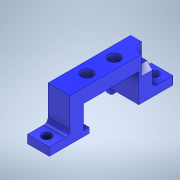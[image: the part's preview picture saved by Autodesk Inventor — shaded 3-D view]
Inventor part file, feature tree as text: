
AUTODESK INVENTOR PART (.ipt)
format: ipt  version: 2022.6 (Build 266554000, 554)  size: 222,208 bytes
history: native  units: mm
features: projected_geometry x6, sketch x5, extrude x4, hole x2, chamfer x2, fillet x1
ambient origin geometry x8: Origin, YZ Plane, XZ Plane, XY Plane, X Axis, Y Axis, Z Axis, Center Point
bodies: Solid1 (feature_tree)
feature tree (20):
  extrude  "Extrusion1"  Depth=5.0mm
  hole  "Hole1"  [1 undecoded]
  extrude  "Extrusion4"  Depth=10.0mm
  fillet  "Fillet1"  Radius=10.5mm
  sketch  "Sketch8"  dims[d9=4.3mm d10=6.0mm d11=4.0mm d12=2.0mm d13=90.0deg d14=10.0mm d15=20.594885mm d16=10.5mm]
  hole  "Hole3"  [1 undecoded]
  extrude  "Extrusion5"  Depth=7.5mm
  chamfer  "Chamfer1"  Distance=3.0mm
  extrude  "Extrusion6"  Depth=7.5mm
  chamfer  "Chamfer2"  Distance=1.5mm
  sketch  "Sketch1"  dims[d0=5.0mm d2=5.0mm]
  sketch  "Sketch2"  dims[d3=20.2mm d4=5.0mm]
  projected_geometry  "Projected Loop1"
  sketch  "Sketch6"  dims[d5=8.0mm d6=0.0mm d8=10.0mm]
  projected_geometry  "Projected Loop4"
  projected_geometry  "Projected Loop7"
  projected_geometry  "Projected Loop8"
  projected_geometry  "Projected Loop9"
  sketch  "Sketch9"  dims[d23=2.0mm d24=2.0mm d31=7.5mm d33=3.0mm d34=0.0mm d35=7.5mm d36=1.5mm d49=3.0mm d50=3.4mm d51=6.0mm d52=4.0mm d53=2.0mm d54=90.0deg d55=10.0mm d56=20.594885mm d58=12.5mm d59=2.0mm d60=2.0mm d61=7.5mm d62=7.5mm d63=3.0mm d64=3.9mm d65=8.0mm d66=5.0mm d67=0.0mm d68=2.0mm d69=2.0mm d70=45.0deg d71=2.9mm d72=3.8mm d73=0.0mm d74=0.8mm d75=2.0mm d76=45.0deg]
  projected_geometry  "Projected Loop10"
note: 2 required parameter values undecoded (feature->parameter linkage not recoverable at this tier; creation-order binding heuristic only, values carry confidence <= 0.55)
